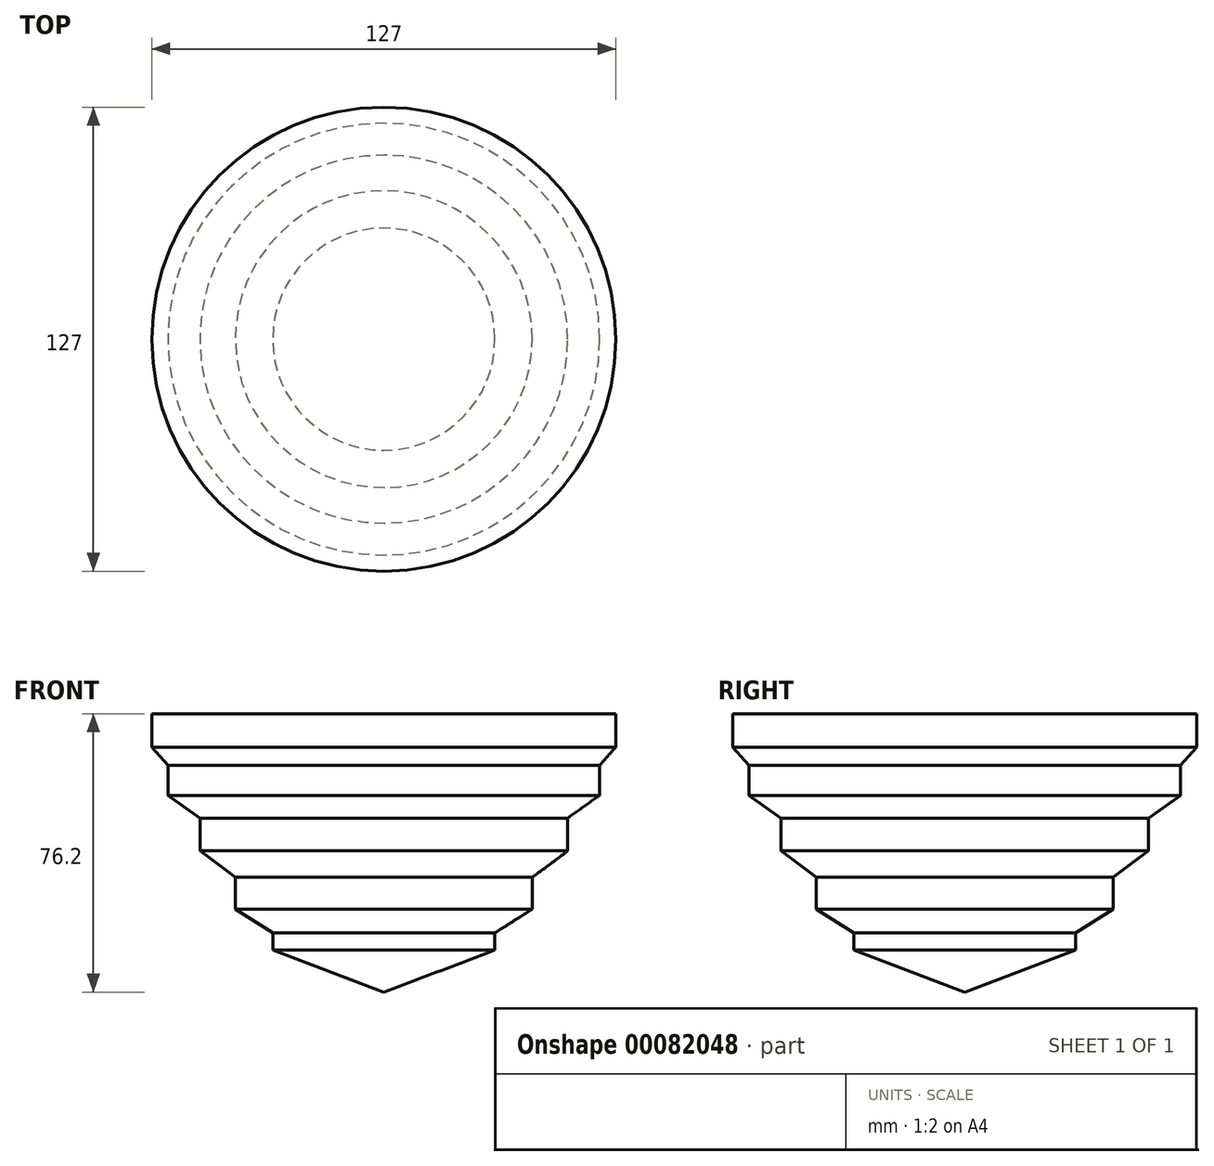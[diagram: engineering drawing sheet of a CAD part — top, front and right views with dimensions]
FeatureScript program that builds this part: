
annotation { "Feature Type Name" : "Feature", "Feature Type Description" : "" }
export const myFeature = defineFeature(function(context is Context, id is Id, definition is map)
    precondition{}
    {
        {
            var Q0;
            Q0=qCreatedBy(makeId("Front.planeOp"),FACE);
            var sketch = newSketch(context, id + "F0", { "sketchPlane" : qUnion([Q0])});
            skLineSegment(sketch, "E0", {"start": v(0, 76.2) * mm, "end": v(63.5, 76.2) * mm});
            skLineSegment(sketch, "E1", {"start": v(63.5, 76.2) * mm, "end": v(63.5, 67.05) * mm});
            skLineSegment(sketch, "E2", {"start": v(63.5, 67.05) * mm, "end": v(59.07, 62.06) * mm});
            skLineSegment(sketch, "E3", {"start": v(59.07, 62.06) * mm, "end": v(59.07, 53.84) * mm});
            skLineSegment(sketch, "E4", {"start": v(59.07, 53.84) * mm, "end": v(50.35, 47.6) * mm});
            skLineSegment(sketch, "E5", {"start": v(50.35, 47.6) * mm, "end": v(50.35, 38.63) * mm});
            skLineSegment(sketch, "E6", {"start": v(50.35, 38.63) * mm, "end": v(40.63, 31.4) * mm});
            skLineSegment(sketch, "E7", {"start": v(40.63, 31.4) * mm, "end": v(40.63, 22.68) * mm});
            skLineSegment(sketch, "E8", {"start": v(40.63, 22.68) * mm, "end": v(30.4, 16.2) * mm});
            skLineSegment(sketch, "E9", {"start": v(30.4, 16.2) * mm, "end": v(30.4, 11.47) * mm});
            skLineSegment(sketch, "E10", {"start": v(30.4, 11.47) * mm, "end": v(0, 0) * mm});
            skLineSegment(sketch, "E11", {"start": v(0, 76.2) * mm, "end": v(0, 0) * mm});
            skSolve(sketch);
        }
        {
            var Q0;
            Q0=makeQuery(id+"F0.imprint","IMPRINT",FACE,{"disambiguationData":[TD([[makeQuery(id+"F0.imprint","IMPRINT",EDGE,{"derivedFrom":sQuery(id+"F0.wireOp",EDGE,"E0")}),-1.0]])]});
            var Q1;
            Q1=sQuery(id+"F0.wireOp",EDGE,"E11");
            revolve(context, id + "F1", {"entities" : qUnion([Q0]), "axis" : qUnion([Q1]), "revolveType" : RevolveType.FULL});
        }
    });
